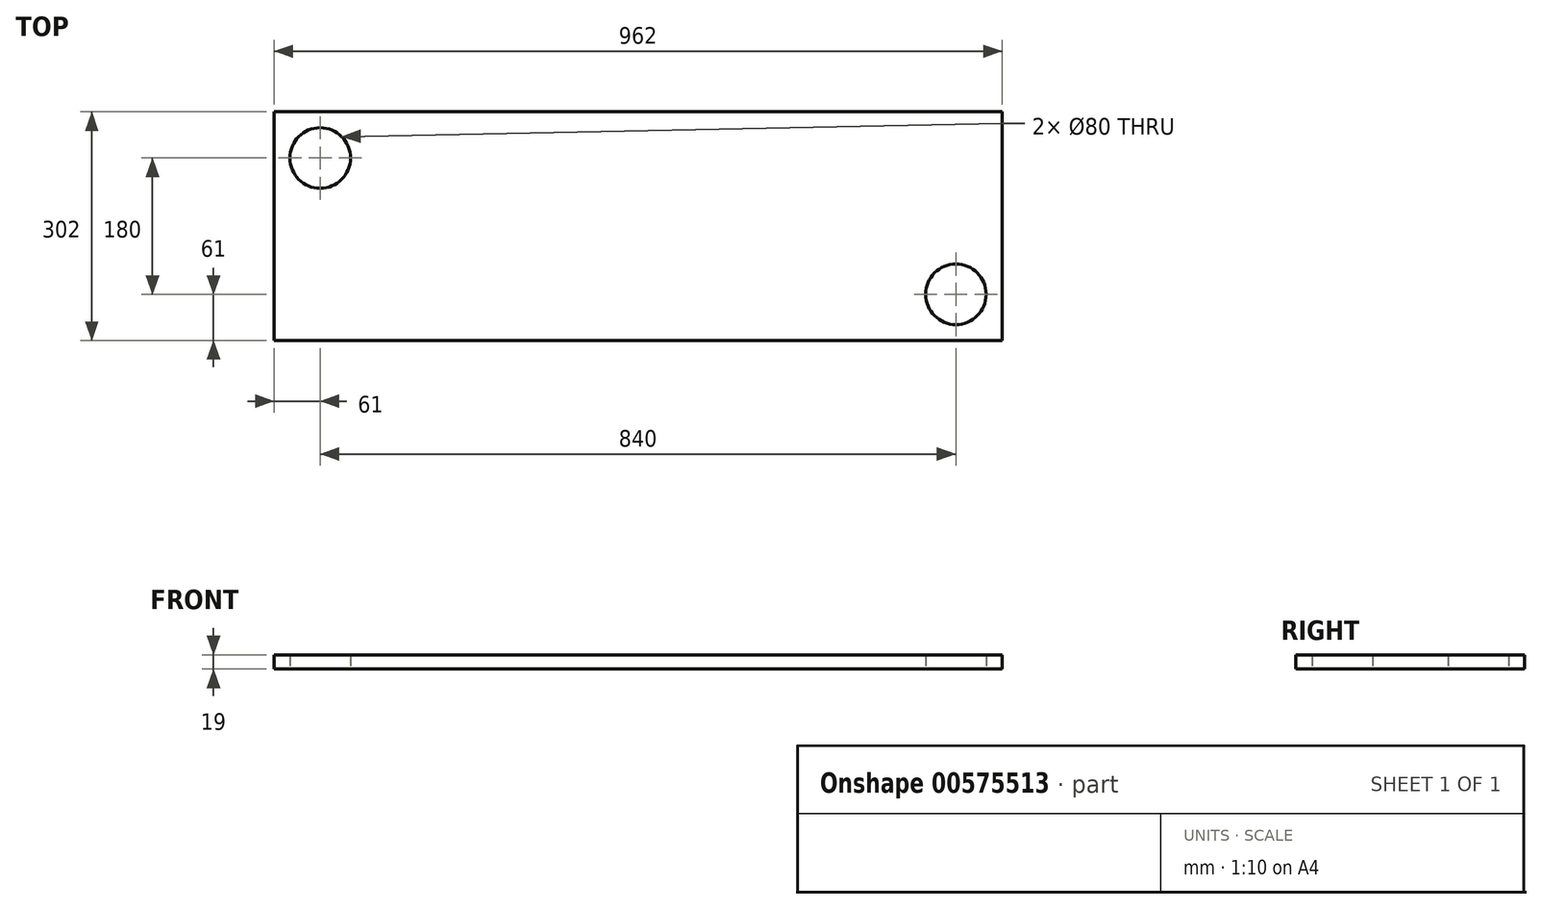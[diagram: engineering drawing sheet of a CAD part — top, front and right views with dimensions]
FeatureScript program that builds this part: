
annotation { "Feature Type Name" : "Feature", "Feature Type Description" : "" }
export const myFeature = defineFeature(function(context is Context, id is Id, definition is map)
    precondition{}
    {
        {
            var Q0;
            Q0=qCreatedBy(makeId("Top.planeOp"),FACE);
            var sketch = newSketch(context, id + "F0", { "sketchPlane" : qUnion([Q0])});
            skPoint(sketch, "E0.middle", {"position": v(0, 0) * mm});
            skLineSegment(sketch, "E1.bottom", {"start": v(500, 170) * mm, "end": v(-500, 170) * mm});
            skLineSegment(sketch, "E1.top", {"start": v(500, -170) * mm, "end": v(-500, -170) * mm});
            skLineSegment(sketch, "E1.left", {"start": v(500, 170) * mm, "end": v(500, -170) * mm});
            skLineSegment(sketch, "E1.right", {"start": v(-500, 170) * mm, "end": v(-500, -170) * mm});
            skCircle(sketch, "E2", {"center": v(-420, 90) * mm, "radius": 40 * mm});
            skCircle(sketch, "E3", {"center": v(420, -90) * mm, "radius": 40 * mm});
            skLineSegment(sketch, "E4.bottom", {"start": v(-481, 151) * mm, "end": v(481, 151) * mm});
            skLineSegment(sketch, "E4.top", {"start": v(-481, -151) * mm, "end": v(481, -151) * mm});
            skLineSegment(sketch, "E4.left", {"start": v(-481, 151) * mm, "end": v(-481, -151) * mm});
            skLineSegment(sketch, "E4.right", {"start": v(481, 151) * mm, "end": v(481, -151) * mm});
            skSolve(sketch);
        }
        {
            var Q0;
            Q0=makeQuery(id+"F0.imprint","IMPRINT",FACE,{"disambiguationData":[TD([[makeQuery(id+"F0.imprint","IMPRINT",EDGE,{"derivedFrom":sQuery(id+"F0.wireOp",EDGE,"E2")}),-1.0]])]});
            extrude(context, id + "F1", {"entities" : qUnion([Q0]), "depth" : 19 * mm, "offsetDistance" : 25 * mm});
        }
    });
